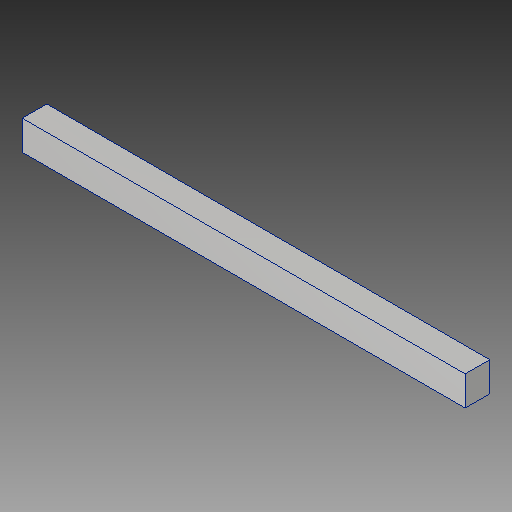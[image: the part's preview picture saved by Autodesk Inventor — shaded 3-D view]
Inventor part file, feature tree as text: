
AUTODESK INVENTOR PART (.ipt)
format: ipt  version: 2019 (Build 230136000, 136)  size: 93,184 bytes
history: native  units: in
note: dims shown in document units (in); Inventor stores cm internally (conversion verified against a paired STEP export)
features: extrude x1, sketch x1
ambient origin geometry x8: Origin, YZ Plane, XZ Plane, XY Plane, X Axis, Y Axis, Z Axis, Center Point
bodies: Solid1 (feature_tree)
feature tree (2):
  extrude  "Extrusion1"  Depth=0.5in
  sketch  "Sketch1"  dims[d0=0.6in d1=0.5in d2=9.0in d3=0.0in]
